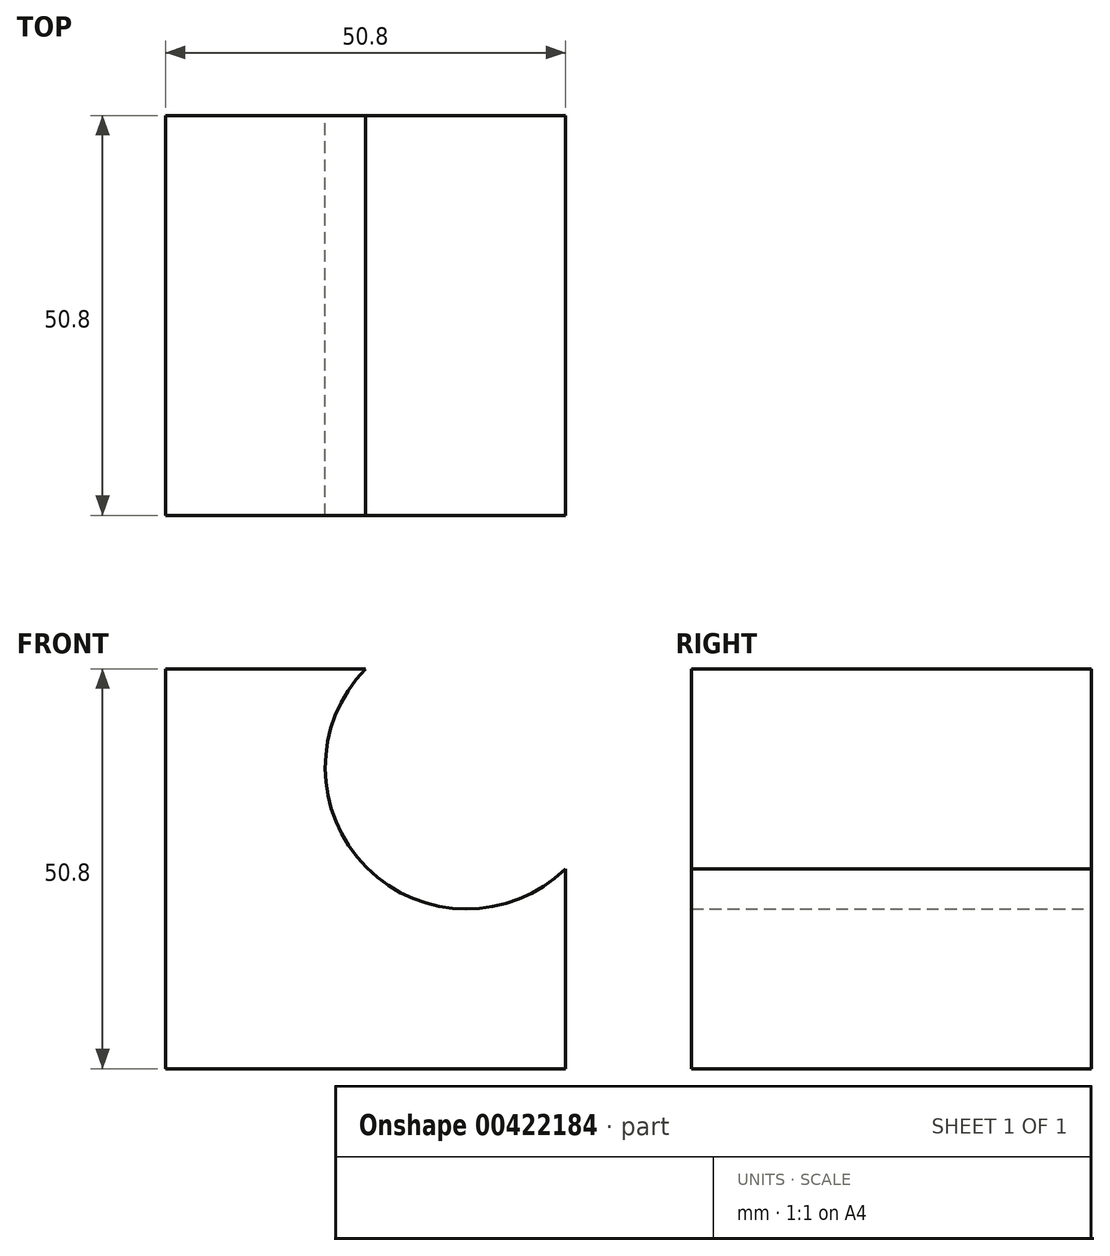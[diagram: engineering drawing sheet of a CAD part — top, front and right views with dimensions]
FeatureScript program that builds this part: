
annotation { "Feature Type Name" : "Feature", "Feature Type Description" : "" }
export const myFeature = defineFeature(function(context is Context, id is Id, definition is map)
    precondition{}
    {
        {
            var Q0;
            Q0=qCreatedBy(makeId("Front.planeOp"),FACE);
            var sketch = newSketch(context, id + "F0", { "sketchPlane" : qUnion([Q0])});
            skLineSegment(sketch, "E0", {"start": v(0, 18.48) * mm, "end": v(-25.4, 18.48) * mm});
            skLineSegment(sketch, "E1", {"start": v(-25.4, 18.48) * mm, "end": v(-25.4, -32.32) * mm});
            skLineSegment(sketch, "E2", {"start": v(-25.4, -32.32) * mm, "end": v(25.4, -32.32) * mm});
            skLineSegment(sketch, "E3", {"start": v(25.4, -32.32) * mm, "end": v(25.4, -6.92) * mm});
            skArc(sketch, "E4", {"start": v(0, 18.48) * mm, "mid": v(0.15, -6.78) * mm, "end": v(25.4, -6.92) * mm});
            skSolve(sketch);
        }
        {
            var Q0;
            Q0 = qSketchRegion(id + "F0", true);
            extrude(context, id + "F1", {"entities" : qUnion([Q0]), "depth" : 50.8 * mm});
        }
    });
